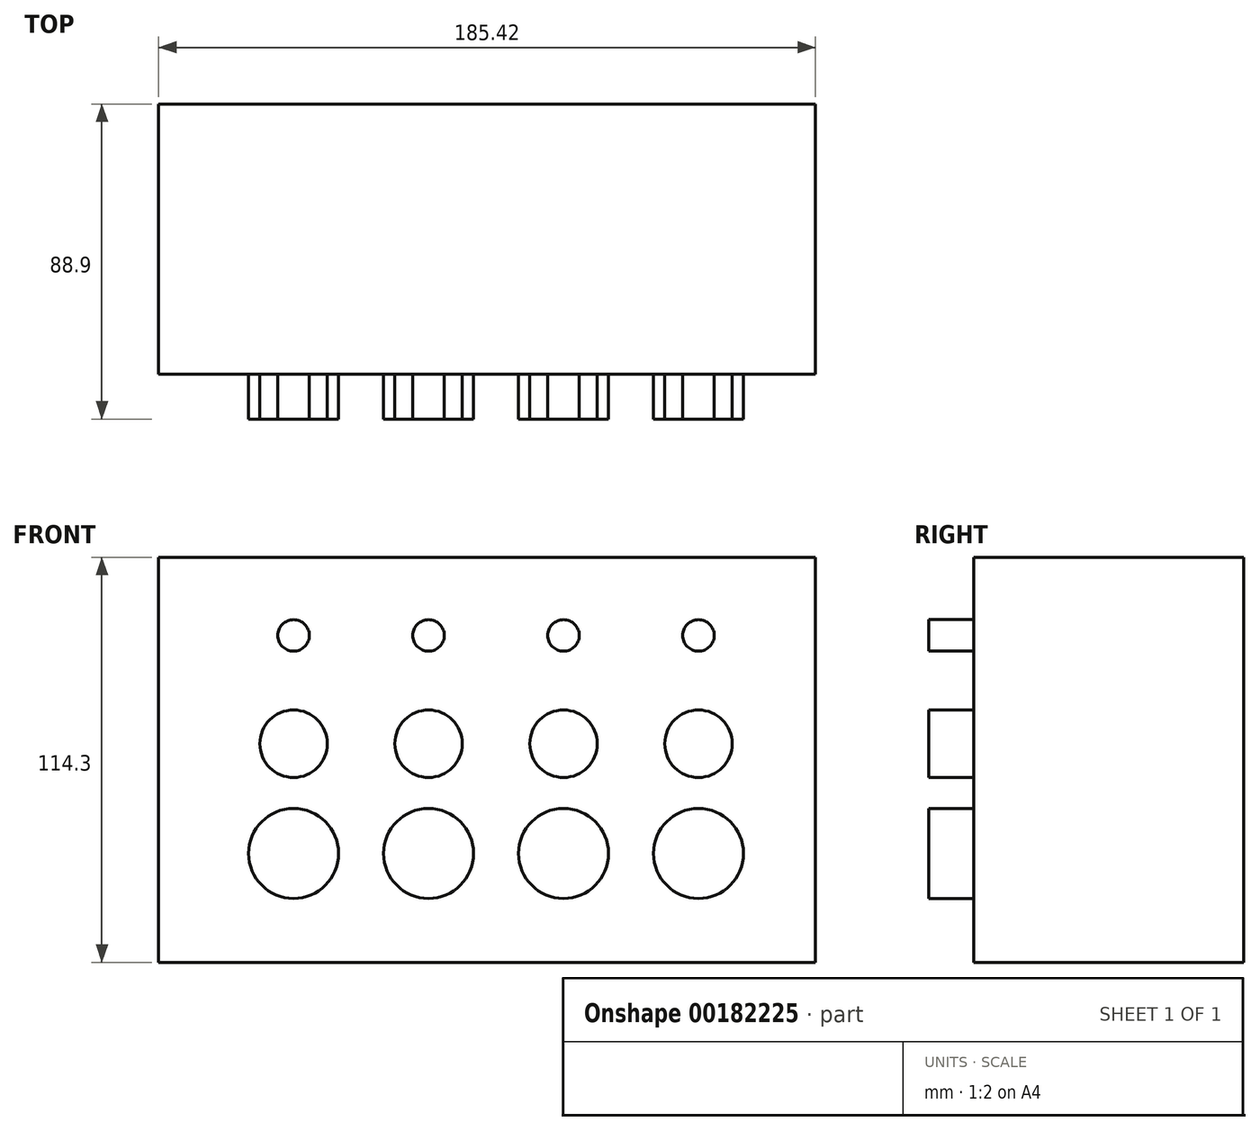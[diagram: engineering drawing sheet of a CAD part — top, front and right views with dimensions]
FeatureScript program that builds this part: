
annotation { "Feature Type Name" : "Feature", "Feature Type Description" : "" }
export const myFeature = defineFeature(function(context is Context, id is Id, definition is map)
    precondition{}
    {
        {
            var Q0;
            Q0=qCreatedBy(makeId("Front.planeOp"),FACE);
            var sketch = newSketch(context, id + "F0", { "sketchPlane" : qUnion([Q0])});
            skLineSegment(sketch, "E0.bottom", {"start": v(185.42, 114.3) * mm, "end": v(0, 114.3) * mm});
            skLineSegment(sketch, "E0.top", {"start": v(185.42, 0) * mm, "end": v(0, 0) * mm});
            skLineSegment(sketch, "E0.left", {"start": v(185.42, 114.3) * mm, "end": v(185.42, 0) * mm});
            skLineSegment(sketch, "E0.right", {"start": v(0, 114.3) * mm, "end": v(0, 0) * mm});
            skSolve(sketch);
        }
        {
            var Q0;
            Q0=makeQuery(id+"F0.imprint","IMPRINT",FACE,{"disambiguationData":[TD([[makeQuery(id+"F0.imprint","IMPRINT",EDGE,{"derivedFrom":sQuery(id+"F0.wireOp",EDGE,"E0.bottom")}),1.0]])]});
            extrude(context, id + "F3", {"entities" : qUnion([Q0]), "oppositeDirection" : true, "depth" : 76.2 * mm});
        }
        {
            var Q0;
            Q0=makeQuery(id+"F3.opExtrude","CAP_FACE",FACE,{"disambiguationData":[OSD([sQuery(id+"F0.wireOp",EDGE,"E0.bottom"),sQuery(id+"F0.wireOp",EDGE,"E0.top"),sQuery(id+"F0.wireOp",EDGE,"E0.left"),sQuery(id+"F0.wireOp",EDGE,"E0.right")])],"isStart":true});
            var sketch = newSketch(context, id + "F1", { "sketchPlane" : qUnion([Q0])});
            skPoint(sketch, "E1", {"position": v(38.1, 92.24) * mm});
            skPoint(sketch, "E2", {"position": v(38.1, 61.67) * mm});
            skPoint(sketch, "E3", {"position": v(38.1, 30.72) * mm});
            skPoint(sketch, "E4", {"position": v(76.2, 92.24) * mm});
            skPoint(sketch, "E5", {"position": v(76.2, 61.67) * mm});
            skPoint(sketch, "E6", {"position": v(76.2, 30.72) * mm});
            skCircle(sketch, "E7", {"center": v(38.1, 92.24) * mm, "radius": 4.45 * mm});
            skCircle(sketch, "E8", {"center": v(38.1, 61.67) * mm, "radius": 9.53 * mm});
            skCircle(sketch, "E9", {"center": v(38.1, 30.72) * mm, "radius": 12.7 * mm});
            skCircle(sketch, "E10", {"center": v(76.2, 92.24) * mm, "radius": 4.45 * mm});
            skCircle(sketch, "E11", {"center": v(76.2, 61.67) * mm, "radius": 9.53 * mm});
            skCircle(sketch, "E12", {"center": v(76.2, 30.72) * mm, "radius": 12.7 * mm});
            skPoint(sketch, "E13", {"position": v(114.3, 92.24) * mm});
            skPoint(sketch, "E14", {"position": v(114.3, 61.67) * mm});
            skPoint(sketch, "E15", {"position": v(114.3, 30.72) * mm});
            skCircle(sketch, "E16", {"center": v(114.3, 92.24) * mm, "radius": 4.45 * mm});
            skCircle(sketch, "E17", {"center": v(114.3, 61.67) * mm, "radius": 9.53 * mm});
            skCircle(sketch, "E18", {"center": v(114.3, 30.72) * mm, "radius": 12.7 * mm});
            skPoint(sketch, "E19", {"position": v(152.4, 92.24) * mm});
            skPoint(sketch, "E20", {"position": v(152.4, 61.67) * mm});
            skPoint(sketch, "E21", {"position": v(152.4, 30.72) * mm});
            skCircle(sketch, "E22", {"center": v(152.4, 92.24) * mm, "radius": 4.45 * mm});
            skCircle(sketch, "E23", {"center": v(152.4, 61.67) * mm, "radius": 9.53 * mm});
            skCircle(sketch, "E24", {"center": v(152.4, 30.72) * mm, "radius": 12.7 * mm});
            skSolve(sketch);
        }
        {
            var Q0;
            Q0=qSketchRegion(id+"F1",true);
            extrude(context, id + "F2", {"entities" : qUnion([Q0]), "operationType" : NewBodyOperationType.ADD, "depth" : 12.7 * mm});
        }
    });
